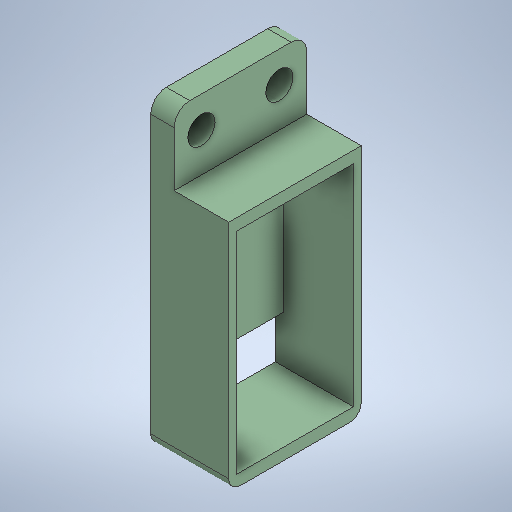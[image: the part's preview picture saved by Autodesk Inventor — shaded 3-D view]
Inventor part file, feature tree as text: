
AUTODESK INVENTOR PART (.ipt)
format: ipt  version: 2025 (Build 290162000, 162)  size: 621,056 bytes
history: native  units: mm
features: extrude x5, sketch x5, fillet x2
ambient origin geometry x8: Origin, YZ Plane, XZ Plane, XY Plane, X Axis, Y Axis, Z Axis, Center Point
bodies: Solide1 (feature_tree)
feature tree (12):
  extrude  "Extrusion1"  Depth=30.0mm
  extrude  "Extrusion2"  Depth=17.0mm
  extrude  "Extrusion3"  Depth=10.0mm TaperAngle=0.0deg
  extrude  "Extrusion4"  Depth=27.0mm
  extrude  "Extrusion5"  Depth=15.0mm
  fillet  "Congé1"  Radius=9.0mm
  fillet  "Congé2"  Radius=6.0mm
  sketch  "Esquisse1"
  sketch  "Esquisse2"
  sketch  "Esquisse3"
  sketch  "Esquisse4"
  sketch  "Esquisse5"
